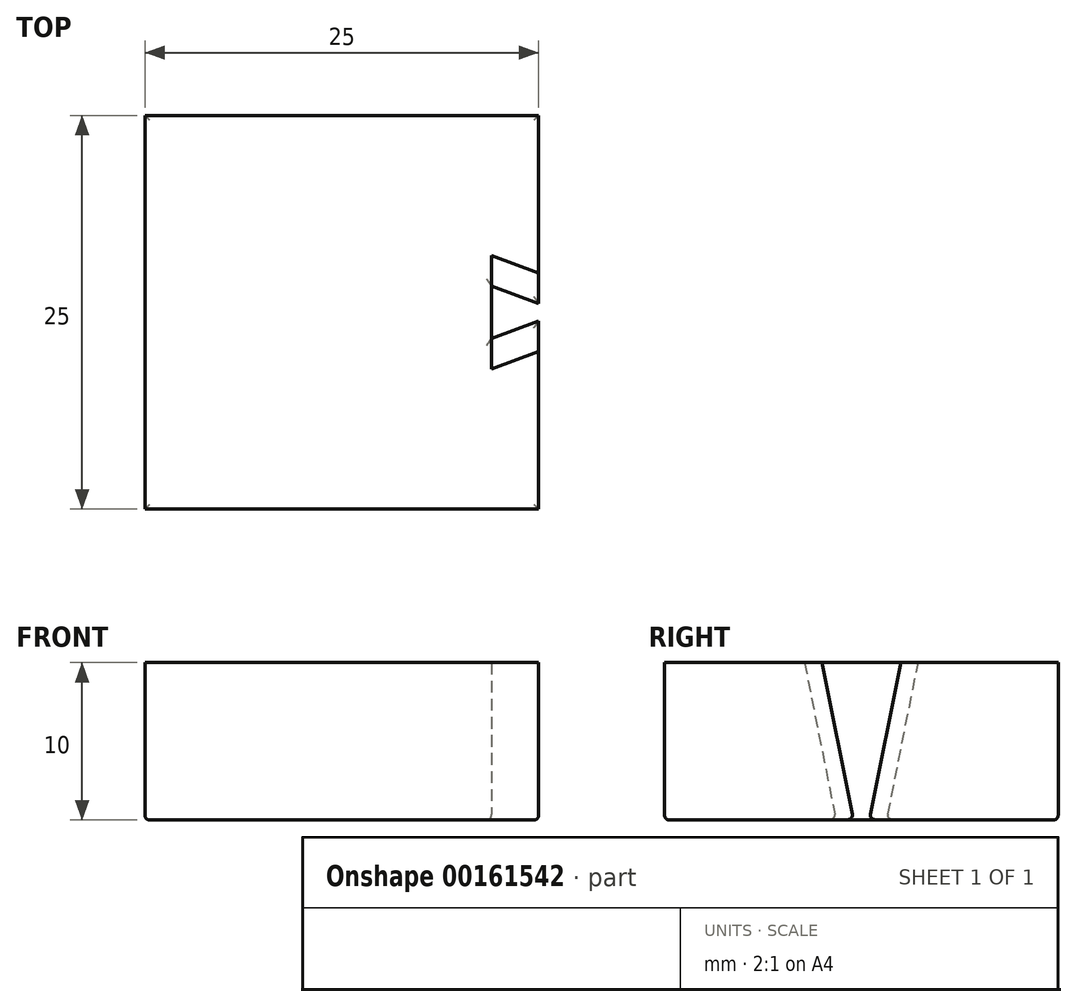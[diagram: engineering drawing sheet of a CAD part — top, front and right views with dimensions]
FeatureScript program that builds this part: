
annotation { "Feature Type Name" : "Feature", "Feature Type Description" : "" }
export const myFeature = defineFeature(function(context is Context, id is Id, definition is map)
    precondition{}
    {
        {
            var Q0;
            Q0=qCreatedBy(makeId("Top.planeOp"),FACE);
            var sketch = newSketch(context, id + "F0", { "sketchPlane" : qUnion([Q0])});
            skLineSegment(sketch, "E0.bottom", {"start": v(12.5, -12.5) * mm, "end": v(-12.5, -12.5) * mm});
            skLineSegment(sketch, "E0.top", {"start": v(12.5, 12.5) * mm, "end": v(-12.5, 12.5) * mm});
            skLineSegment(sketch, "E0.left", {"start": v(12.5, -12.5) * mm, "end": v(12.5, 12.5) * mm});
            skLineSegment(sketch, "E0.right", {"start": v(-12.5, -12.5) * mm, "end": v(-12.5, 12.5) * mm});
            skPoint(sketch, "E0.middle", {"position": v(0, 0) * mm});
            skSolve(sketch);
        }
        {
            var Q0;
            Q0=makeQuery(id+"F0.imprint","IMPRINT",FACE,{"disambiguationData":[TD([[makeQuery(id+"F0.imprint","IMPRINT",EDGE,{"derivedFrom":sQuery(id+"F0.wireOp",EDGE,"E0.bottom")}),-1.0]])]});
            extrude(context, id + "F1", {"entities" : qUnion([Q0]), "depth" : 8 * mm * 1.25});
        }
        {
            var Q0;
            Q0=makeQuery(id+"F1.opExtrude","SWEPT_FACE",FACE,{"disambiguationData":[OSD([sQuery(id+"F0.wireOp",EDGE,"E0.left")])]});
            var sketch = newSketch(context, id + "F2", { "sketchPlane" : qUnion([Q0])});
            skLineSegment(sketch, "E1", {"start": v(-2.5, 10) * mm, "end": v(-0.5, 0) * mm});
            skLineSegment(sketch, "E2", {"start": v(-0.5, 0) * mm, "end": v(0.5, 0) * mm});
            skLineSegment(sketch, "E3", {"start": v(0.5, 0) * mm, "end": v(2.5, 10) * mm});
            skLineSegment(sketch, "E4", {"start": v(2.5, 10) * mm, "end": v(-2.5, 10) * mm});
            skLineSegment(sketch, "E5", {"start": v(0, 0) * mm, "end": v(0, 10) * mm, "construction": true});
            skSolve(sketch);
        }
        {
            var Q0;
            Q0 = qSketchRegion(id + "F2", true);
            extrude(context, id + "F3", {"entities" : qUnion([Q0]), "operationType" : NewBodyOperationType.REMOVE, "oppositeDirection" : true, "depth" : 3 * mm, "hasDraft" : true, "draftAngle" : 20 * degree});
        }
        {
            var Q0;
            Q0=makeQuery(id+"F1.opExtrude","CAP_FACE",FACE,{"disambiguationData":[OSD([sQuery(id+"F0.wireOp",EDGE,"E0.bottom"),sQuery(id+"F0.wireOp",EDGE,"E0.top"),sQuery(id+"F0.wireOp",EDGE,"E0.left"),sQuery(id+"F0.wireOp",EDGE,"E0.right")])],"isStart":true});
            fillet(context, id + "F4", {"entities" : qUnion([Q0]), "radius" : .3 * mm, "tangentPropagation" : true, "allowEdgeOverflow" : false});
        }
    });
